# Revit family: bimlib_narujnyeblokisistemakondicionirovaniya_mrv-iii-s_seriyaau_haier
name_source: partatom
category: Оборудование
units: mm (PartAtom-declared; Revit-internal decimal feet)

## family parameters
Всегда вертикально = Да
На основе рабочей плоскости = Нет
Общий = Нет
При загрузке вырезать с полостями = Нет
Размер круглого соединителя = Использовать диаметр
Тип детали = Нормальный
Точка расчета площади = Нет

## types (6) — shared parameters
ADSK_URL документации изделия = https://haierproff.ru
ADSK_URL страницы изделия = https://haierproff.ru
ADSK_Версия Revit = 2017
ADSK_Группирование = VRF-системы MRV III - S'' серия AU
ADSK_Единица измерения = шт.
ADSK_Завод-изготовитель = Haier Group
ADSK_Классификация нагрузок = ОВК
ADSK_Количество = 1
ADSK_Коэффициент мощности = 1
ADSK_Масса = 108
ADSK_Обозначение = MRV III - S'' серия AU
ADSK_Размер_Высота = 1340 мм
ADSK_Размер_Глубина = 370 мм
ADSK_Размер_Ширина = 950 мм
ADSK_Расход воздуха = 7200.0 м³/ч
BL_BIM library = https://bimlib.pro
HG_URL поставщика = www.haierproff.ru
URL = www.haier.com
Диаметр_Газ = 15.88 мм
Диаметр_Жидкость = 9.52 мм
Заправка хладагента = 4.00 кг
Изготовитель = Haier Group
Производитель компрессора = MITSUBISHI ELECTRIC
Работа на обогрев = Нет
Рабочий диапазон_Обогрев = -20 ~ 27
Рабочий диапазон_Охлаждение = -15 ~ 48
Сбоку = Подключение : Сбоку
Сзади = Подключение : Сзади
Снизу = Подключение : Снизу
Спереди = Подключение : Спереди
Тип компрессора = Роторный
Тип хладагента = R410A
Частота тока = 50 Гц
zero-valued in all types: Отметка по умолчанию

## per-type parameters (varying)
| type | ADSK_Код изделия | ADSK_Количество фаз | ADSK_Наименование | ADSK_Наименование краткое | ADSK_Напряжение | ADSK_Номинальная мощность | ADSK_Полная мощность | Звуковая мощность | Звуковое давление | Обогрев_Потребляемая мощность | Охлаждение_Потребляемая мощность | Теплопроизводительность | Холодопроизводительность |
| AU042FPERA_4HP_HAIER | AU042FPERA | 1 | Наружный блок VRF-системы кондиционирования MRV III - S'' серия AU, 4HP | VRF-системы MRV MRV III - S'' серия AU, 4HP | 230 В | 2990 Вт | 2990 В·А | 68 | 57 | 3 кВт | 3 кВт | 14 кВт | 12 кВт |
| AU04IFPERA_4HP_HAIER | AU04IFPERA | 3 | Наружный блок VRF-системы кондиционирования MRV III - S'' серия AU, 4HP | VRF-системы MRV MRV III - S'' серия AU, 4HP | 400 В | 2990 Вт | 2990 В·А | 68 | 57 | 3 кВт | 3 кВт | 14 кВт | 12 кВт |
| AU052FPERA_5HP_HAIER | AU052FPERA | 1 | Наружный блок VRF-системы кондиционирования MRV III - S'' серия AU, 5HP | VRF-системы MRV MRV III - S'' серия AU, 5HP | 230 В | 3510 Вт | 3510 В·А | 69 | 58 | 4 кВт | 4 кВт | 16 кВт | 14 кВт |
| AU05IFPERA_5HP_HAIER | AU05IFPERA | 3 | Наружный блок VRF-системы кондиционирования MRV III - S'' серия AU, 5HP | VRF-системы MRV MRV III - S'' серия AU, 5HP | 400 В | 3510 Вт | 3510 В·А | 69 | 58 | 4 кВт | 4 кВт | 16 кВт | 14 кВт |
| AU062FPERA_6HP_HAIER | AU062FPERA | 1 | Наружный блок VRF-системы кондиционирования MRV III - S'' серия AU, 6HP | VRF-системы MRV MRV III - S'' серия AU, 6HP | 230 В | 4310 Вт | 4310 В·А | 70 | 59 | 4 кВт | 4 кВт | 18 кВт | 16 кВт |
| AU06IFPERA_6HP_HAIER | AU06IFPERA | 3 | Наружный блок VRF-системы кондиционирования MRV III - S'' серия AU, 6HP | VRF-системы MRV MRV III - S'' серия AU, 6HP | 400 В | 4310 Вт | 4310 В·А | 70 | 59 | 4 кВт | 4 кВт | 18 кВт | 16 кВт |
